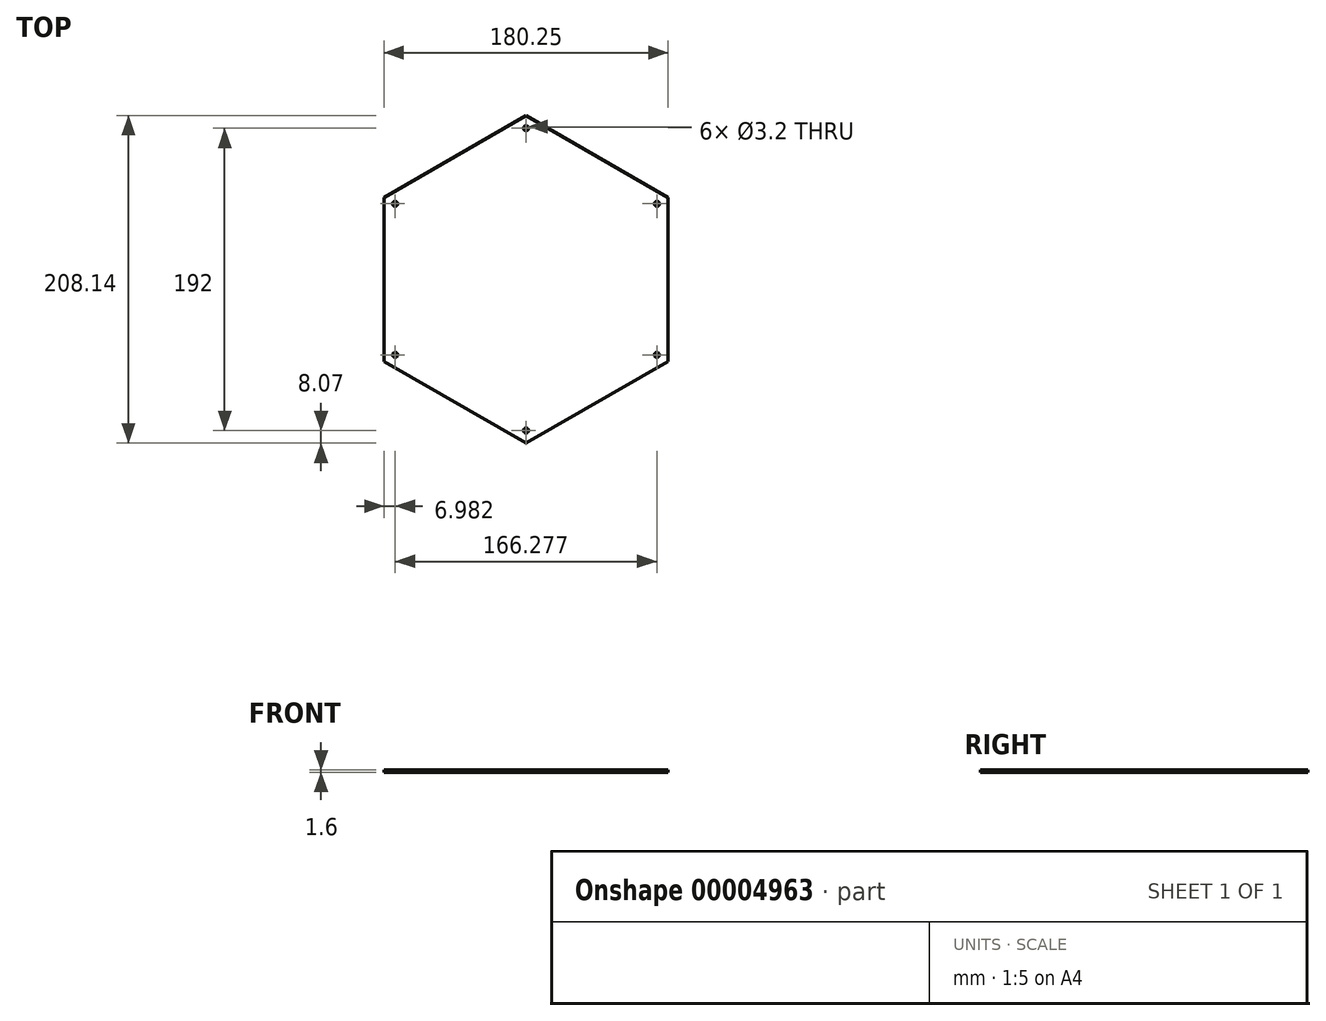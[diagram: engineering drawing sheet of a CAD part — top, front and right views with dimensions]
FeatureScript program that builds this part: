
annotation { "Feature Type Name" : "Feature", "Feature Type Description" : "" }
export const myFeature = defineFeature(function(context is Context, id is Id, definition is map)
    precondition{}
    {
        {
            var Q0;
            Q0=qCreatedBy(makeId("Top.planeOp"),FACE);
            var sketch = newSketch(context, id + "F0", { "sketchPlane" : qUnion([Q0])});
            skLineSegment(sketch, "E0", {"start": v(0, 0) * mm, "end": v(0, 104.07) * mm, "construction": true});
            skLineSegment(sketch, "E1", {"start": v(0, 0) * mm, "end": v(90.12, 52.03) * mm, "construction": true});
            skCircle(sketch, "E2", {"center": v(0, 0) * mm, "radius": 85 * mm, "construction": true});
            skLineSegment(sketch, "E3", {"start": v(0, 104.07) * mm, "end": v(90.13, 52.03) * mm});
            skCircle(sketch, "E4", {"center": v(0, 96) * mm, "radius": 1.6 * mm});
            skCircle(sketch, "E5.1.0", {"center": v(-83.14, 48) * mm, "radius": 1.6 * mm});
            skLineSegment(sketch, "E5.1.1", {"start": v(-90.13, 52.03) * mm, "end": v(0, 104.07) * mm});
            skCircle(sketch, "E5.2.0", {"center": v(-83.14, -48) * mm, "radius": 1.6 * mm});
            skLineSegment(sketch, "E5.2.1", {"start": v(-90.12, -52.03) * mm, "end": v(-90.13, 52.03) * mm});
            skCircle(sketch, "E5.3.0", {"center": v(0, -96) * mm, "radius": 1.6 * mm});
            skLineSegment(sketch, "E5.3.1", {"start": v(0, -104.07) * mm, "end": v(-90.13, -52.03) * mm});
            skCircle(sketch, "E5.4.0", {"center": v(83.14, -48) * mm, "radius": 1.6 * mm});
            skLineSegment(sketch, "E5.4.1", {"start": v(90.12, -52.03) * mm, "end": v(0, -104.07) * mm});
            skCircle(sketch, "E5.5.0", {"center": v(83.14, 48) * mm, "radius": 1.6 * mm});
            skLineSegment(sketch, "E5.5.1", {"start": v(90.12, 52.03) * mm, "end": v(90.13, -52.03) * mm});
            skSolve(sketch);
        }
        {
            var Q0;
            Q0 = qSketchRegion(id + "F0", true);
            extrude(context, id + "F1", {"entities" : qUnion([Q0]), "depth" : 1.6 * mm});
        }
    });
